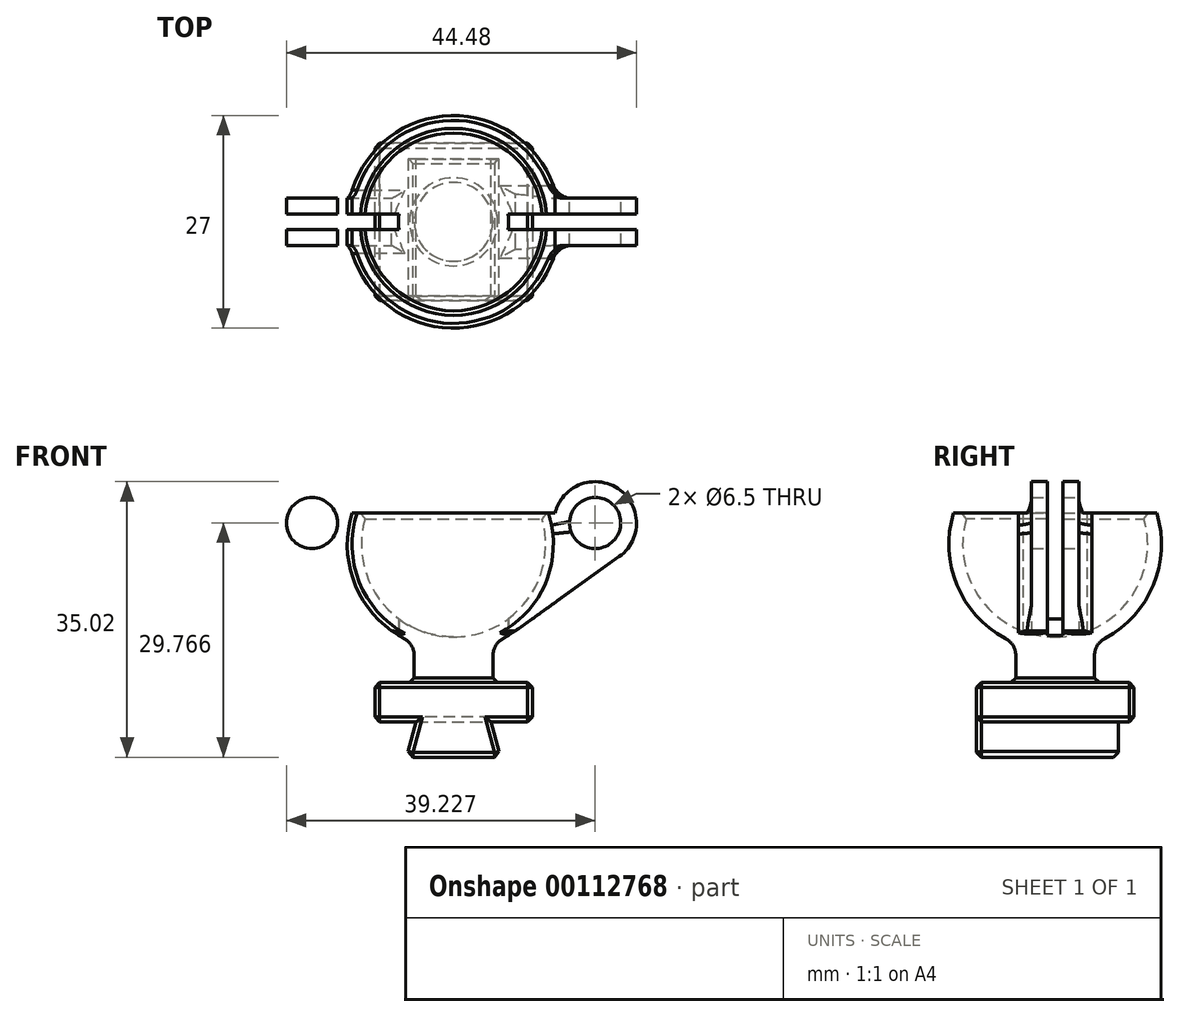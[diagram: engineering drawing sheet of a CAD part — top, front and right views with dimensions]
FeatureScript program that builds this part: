
annotation { "Feature Type Name" : "Feature", "Feature Type Description" : "" }
export const myFeature = defineFeature(function(context is Context, id is Id, definition is map)
    precondition{}
    {
        {
            assignVariable(context, id + "F0", {"name" : "BallWallThickness", "anyValue" : 2});
        }
        {
            assignVariable(context, id + "F1", {"name" : "DovetailBackstopDepth", "anyValue" : 2});
        }
        {
            assignVariable(context, id + "F2", {"name" : "DovetailHeight", "anyValue" : 5});
        }
        {
            assignVariable(context, id + "F3", {"name" : "Thickness", "anyValue" : 20});
        }
        {
            var Q0;
            Q0=qCreatedBy(makeId("Front.planeOp"),FACE);
            var sketch = newSketch(context, id + "F4", { "sketchPlane" : qUnion([Q0])});
            skLineSegment(sketch, "E0", {"start": v(20, 0) * mm, "end": v(20, 5) * mm});
            skLineSegment(sketch, "E1", {"start": v(20, 5) * mm, "end": v(0, 5) * mm});
            skLineSegment(sketch, "E2", {"start": v(5, 5) * mm, "end": v(5, 10) * mm});
            skLineSegment(sketch, "E3", {"start": v(5, 10) * mm, "end": v(15, 10) * mm});
            skLineSegment(sketch, "E4", {"start": v(15, 10) * mm, "end": v(15, 5) * mm});
            skLineSegment(sketch, "E5", {"start": v(10, 5) * mm, "end": v(10, -4.5) * mm, "construction": true});
            skArc(sketch, "E6", {"start": v(-2.9, 26.54) * mm, "mid": v(-2.18, 16.73) * mm, "end": v(5, 10) * mm});
            skPoint(sketch, "E6.centerSnap0", {"position": v(10, 10) * mm});
            skArc(sketch, "E7.trimOffspring", {"start": v(15, 10) * mm, "mid": v(22.18, 16.73) * mm, "end": v(22.9, 26.54) * mm});
            skLineSegment(sketch, "E8", {"start": v(10, 26.54) * mm, "end": v(10, 5) * mm});
            skArc(sketch, "E9", {"start": v(-1.05, 26.54) * mm, "mid": v(10, 10.79) * mm, "end": v(21.05, 26.54) * mm});
            skLineSegment(sketch, "E10", {"start": v(5.25, 0) * mm, "end": v(4.04, -4.5) * mm});
            skLineSegment(sketch, "E11", {"start": v(4.04, -4.5) * mm, "end": v(15.96, -4.5) * mm});
            skLineSegment(sketch, "E12.MirrorCS", {"start": v(14.75, 0) * mm, "end": v(15.96, -4.5) * mm});
            skLineSegment(sketch, "E13", {"start": v(14.75, 0) * mm, "end": v(20, 0) * mm});
            skLineSegment(sketch, "E14", {"start": v(5.25, 0) * mm, "end": v(0, 0) * mm});
            skLineSegment(sketch, "E15", {"start": v(0, 0) * mm, "end": v(0, 5) * mm});
            skLineSegment(sketch, "E16", {"start": v(-3.5, 22.54) * mm, "end": v(23.5, 22.54) * mm, "construction": true});
            skLineSegment(sketch, "E17", {"start": v(22.9, 26.54) * mm, "end": v(-2.9, 26.54) * mm});
            skLineSegment(sketch, "E18", {"start": v(5.25, 0) * mm, "end": v(14.75, 0) * mm});
            skCircle(sketch, "E19", {"center": v(27.99, 25.27) * mm, "radius": 3.25 * mm});
            skArc(sketch, "E20.0", {"start": v(31.04, 21) * mm, "mid": v(30.94, 29.6) * mm, "end": v(22.9, 26.54) * mm});
            skLineSegment(sketch, "E21", {"start": v(31.04, 21) * mm, "end": v(17.86, 11.56) * mm});
            skCircle(sketch, "E22.MirrorC", {"center": v(-7.99, 25.27) * mm, "radius": 3.25 * mm});
            skLineSegment(sketch, "E23.MirrorCS", {"start": v(-11.04, 21) * mm, "end": v(2.14, 11.56) * mm});
            skArc(sketch, "E24.MirrorCS", {"start": v(-11.04, 21) * mm, "mid": v(-10.94, 29.6) * mm, "end": v(-2.9, 26.54) * mm});
            skLineSegment(sketch, "E25", {"start": v(17.86, 11.56) * mm, "end": v(16.84, 12.98) * mm});
            skLineSegment(sketch, "E26.MirrorCS", {"start": v(2.14, 11.56) * mm, "end": v(3.16, 12.98) * mm});
            skSolve(sketch);
        }
        {
            var Q0;
            Q0=makeQuery(id+"F4.imprint","IMPRINT",FACE,{"disambiguationData":[TD([[makeQuery(id+"F4.imprint","IMPRINT",EDGE,{"derivedFrom":sQuery(id+"F4.wireOp",EDGE,"E10")}),1.0]])]});
            extrude(context, id + "F5", {"entities" : qUnion([Q0]), "depth" : (getVariable(context, 'Thickness') / 2) * mm, "hasSecondDirection" : true, "secondDirectionOppositeDirection" : true, "secondDirectionDepth" : (getVariable(context, 'Thickness') / 2 - getVariable(context, 'DovetailBackstopDepth')) * mm});
        }
        {
            var Q0;
            {var subQ4=sQuery(id+"F4.wireOp",EDGE,"E0");Q0=makeQuery(id+"F4.imprint","IMPRINT",FACE,{"disambiguationData":[TD([[makeQuery(id+"F4.imprint","IMPRINT",EDGE,{"derivedFrom":subQ4}),1.0]])]});}
            extrude(context, id + "F6", {"entities" : qUnion([Q0]), "operationType" : NewBodyOperationType.ADD, "depth" : (getVariable(context, 'Thickness')) * mm, "symmetric" : true});
        }
        {
            var Q0;
            {var subQ0=sQuery(id+"F4.wireOp",EDGE,"E2");Q0=makeQuery(id+"F4.imprint","IMPRINT",FACE,{"disambiguationData":[TD([[makeQuery(id+"F4.imprint","IMPRINT",EDGE,{"derivedFrom":subQ0}),-1.0]])]});}
            var Q1;
            Q1=sQuery(id+"F4.wireOp",EDGE,"E8");
            revolve(context, id + "F7", {"operationType" : NewBodyOperationType.ADD, "entities" : qUnion([Q0]), "axis" : qUnion([Q1]), "revolveType" : RevolveType.FULL});
        }
        {
            var Q0;
            Q0=makeQuery(id+"F7.opRevolve","SWEPT_FACE",FACE,{"disambiguationData":[OSD([sQuery(id+"F4.wireOp",EDGE,"E3")])]});
            var sketch = newSketch(context, id + "F8", { "sketchPlane" : qUnion([Q0])});
            skCircle(sketch, "E27", {"center": v(10, 0) * mm, "radius": 13.5 * mm});
            skCircle(sketch, "E28.0", {"center": v(10, 0) * mm, "radius": 5 * mm});
            skLineSegment(sketch, "E29", {"start": v(10, 13.5) * mm, "end": v(10, -13.5) * mm, "construction": true});
            skLineSegment(sketch, "E30", {"start": v(9.5, 13.5) * mm, "end": v(9.5, 6.98) * mm, "construction": true});
            skLineSegment(sketch, "E31.MirrorCS", {"start": v(10.5, 13.5) * mm, "end": v(10.5, 6.98) * mm, "construction": true});
            skLineSegment(sketch, "E32.trimOffspring", {"start": v(9.5, -6.98) * mm, "end": v(9.5, -13.5) * mm, "construction": true});
            skLineSegment(sketch, "E33.trimOffspring", {"start": v(10.5, -6.98) * mm, "end": v(10.5, -13.5) * mm, "construction": true});
            skLineSegment(sketch, "E34", {"start": v(-3.5, 0) * mm, "end": v(23.5, 0) * mm, "construction": true});
            skLineSegment(sketch, "E35", {"start": v(-3.46, 1) * mm, "end": v(3.07, 1) * mm});
            skLineSegment(sketch, "E36.MirrorCS", {"start": v(-3.46, -1) * mm, "end": v(3.07, -1) * mm});
            skLineSegment(sketch, "E37.trimOffspring", {"start": v(16.93, -1) * mm, "end": v(23.46, -1) * mm});
            skLineSegment(sketch, "E38.trimOffspring", {"start": v(16.93, 1) * mm, "end": v(23.46, 1) * mm});
            skCircle(sketch, "E39.0", {"center": v(10, 0) * mm, "radius": 7 * mm});
            skLineSegment(sketch, "E40", {"start": v(-3.46, -1) * mm, "end": v(-33.46, -1) * mm});
            skLineSegment(sketch, "E41", {"start": v(-33.46, -1) * mm, "end": v(-33.46, 1) * mm});
            skLineSegment(sketch, "E42", {"start": v(-33.46, 1) * mm, "end": v(-3.46, 1) * mm});
            skLineSegment(sketch, "E43.MirrorCS", {"start": v(53.46, 1) * mm, "end": v(23.46, 1) * mm});
            skLineSegment(sketch, "E44.MirrorCS", {"start": v(23.46, -1) * mm, "end": v(53.46, -1) * mm});
            skLineSegment(sketch, "E45.MirrorCS", {"start": v(53.46, -1) * mm, "end": v(53.46, 1) * mm});
            skSolve(sketch);
        }
        {
            var Q0;
            {var subQ6=sQuery(id+"F4.wireOp",EDGE,"E6");Q0=makeQuery(id+"F4.imprint","IMPRINT",FACE,{"disambiguationData":[TD([[makeQuery(id+"F4.imprint","IMPRINT",EDGE,{"derivedFrom":subQ6}),1.0]])]});}
            var Q1;
            {var subQ0=sQuery(id+"F4.wireOp",EDGE,"E26.MirrorCS");Q1=makeQuery(id+"F4.imprint","IMPRINT",FACE,{"disambiguationData":[TD([[makeQuery(id+"F4.imprint","IMPRINT",EDGE,{"derivedFrom":subQ0}),-1.0]])]});}
            var Q2;
            Q2=sQuery(id+"F4.wireOp",EDGE,"E8");
            revolve(context, id + "F9", {"operationType" : NewBodyOperationType.ADD, "entities" : qUnion([Q0, Q1]), "axis" : qUnion([Q2]), "revolveType" : RevolveType.FULL});
        }
        {
            var Q0;
            Q0=makeQuery(id+"F4.imprint","IMPRINT",FACE,{"disambiguationData":[TD([[makeQuery(id+"F4.imprint","IMPRINT",EDGE,{"derivedFrom":sQuery(id+"F4.wireOp",EDGE,"E22.MirrorC")}),1.0]])]});
            var Q1;
            {var subQ3=sQuery(id+"F4.wireOp",EDGE,"E26.MirrorCS");Q1=makeQuery(id+"F4.imprint","IMPRINT",FACE,{"disambiguationData":[TD([[makeQuery(id+"F4.imprint","IMPRINT",EDGE,{"derivedFrom":subQ3}),1.0]])]});}
            var Q2;
            {var subQ3=sQuery(id+"F4.wireOp",EDGE,"E25");Q2=makeQuery(id+"F4.imprint","IMPRINT",FACE,{"disambiguationData":[TD([[makeQuery(id+"F4.imprint","IMPRINT",EDGE,{"derivedFrom":subQ3}),-1.0]])]});}
            var Q3;
            Q3=makeQuery(id+"F4.imprint","IMPRINT",FACE,{"disambiguationData":[TD([[makeQuery(id+"F4.imprint","IMPRINT",EDGE,{"derivedFrom":sQuery(id+"F4.wireOp",EDGE,"E19")}),-1.0]])]});
            extrude(context, id + "F10", {"entities" : qUnion([Q0, Q1, Q2, Q3]), "operationType" : NewBodyOperationType.ADD, "depth" : (3 * getVariable(context, 'BallWallThickness')) * mm, "symmetric" : true});
        }
        {
            var Q0;
            {var subQ0=sQuery(id+"F8.wireOp",EDGE,"E35");Q0=makeQuery(id+"F8.imprint","IMPRINT",FACE,{"disambiguationData":[TD([[makeQuery(id+"F8.imprint","IMPRINT",EDGE,{"derivedFrom":subQ0}),-1.0]])]});}
            var Q1;
            {var subQ0=sQuery(id+"F8.wireOp",EDGE,"E32.trimOffspring");Q1=makeQuery(id+"F8.imprint","IMPRINT",FACE,{"disambiguationData":[TD([[makeQuery(id+"F8.imprint","IMPRINT",EDGE,{"derivedFrom":subQ0}),1.0]])]});}
            var Q2;
            {var subQ0=sQuery(id+"F8.wireOp",EDGE,"E37.trimOffspring");Q2=makeQuery(id+"F8.imprint","IMPRINT",FACE,{"disambiguationData":[TD([[makeQuery(id+"F8.imprint","IMPRINT",EDGE,{"derivedFrom":subQ0}),1.0]])]});}
            var Q3;
            {var subQ0=sQuery(id+"F8.wireOp",EDGE,"E30");Q3=makeQuery(id+"F8.imprint","IMPRINT",FACE,{"disambiguationData":[TD([[makeQuery(id+"F8.imprint","IMPRINT",EDGE,{"derivedFrom":subQ0}),1.0]])]});}
            var Q4;
            {var subQ2=sQuery(id+"F8.wireOp",EDGE,"E40");Q4=makeQuery(id+"F8.imprint","IMPRINT",FACE,{"disambiguationData":[TD([[makeQuery(id+"F8.imprint","IMPRINT",EDGE,{"derivedFrom":subQ2}),-1.0]])]});}
            var Q5;
            {var subQ2=sQuery(id+"F8.wireOp",EDGE,"E43.MirrorCS");Q5=makeQuery(id+"F8.imprint","IMPRINT",FACE,{"disambiguationData":[TD([[makeQuery(id+"F8.imprint","IMPRINT",EDGE,{"derivedFrom":subQ2}),1.0]])]});}
            extrude(context, id + "F11", {"entities" : qUnion([Q0, Q1, Q2, Q3, Q4, Q5]), "operationType" : NewBodyOperationType.REMOVE, "depth" : 25 * mm});
        }
        {
            var Q0;
            {var subQ0=sQuery(id+"F4.wireOp",EDGE,"E6");var subQ1=sQuery(id+"F4.wireOp",EDGE,"E3");var subQ2=sQuery(id+"F4.wireOp",EDGE,"E2");Q0=makeQuery(id+"F9.boolean.opBoolean","MERGE",EDGE,{"derivedFrom":[makeQuery(id+"F7.opRevolve","SWEPT_EDGE",EDGE,{"disambiguationData":[OSD([subQ2,subQ1,subQ0])]}),makeQuery(id+"F9.opRevolve","SWEPT_EDGE",EDGE,{"disambiguationData":[OSD([subQ2,subQ1,subQ0])]})]});}
            var Q1;
            Q1=makeQuery(id+"F7.opRevolve","SWEPT_EDGE",EDGE,{"disambiguationData":[OSD([sQuery(id+"F4.wireOp",EDGE,"E1"),sQuery(id+"F4.wireOp",EDGE,"E2")])]});
            var Q2;
            Q2=makeQuery(id+"F10.boolean.opBoolean","INTERSECT",EDGE,{"disambiguationData":[OD(1.0)],"derivedFrom":[makeQuery(id+"F9.opRevolve","SWEPT_FACE",FACE,{"disambiguationData":[OSD([sQuery(id+"F4.wireOp",EDGE,"E6")])]}),makeQuery(id+"F10.opExtrude","SWEPT_FACE",FACE,{"disambiguationData":[OSD([sQuery(id+"F4.wireOp",EDGE,"E26.MirrorCS")])]})]});
            var Q3;
            Q3=makeQuery(id+"F10.boolean.opBoolean","INTERSECT",EDGE,{"disambiguationData":[OD(1.0)],"derivedFrom":[makeQuery(id+"F9.opRevolve","SWEPT_FACE",FACE,{"disambiguationData":[OSD([sQuery(id+"F4.wireOp",EDGE,"E6")])]}),makeQuery(id+"F10.opExtrude","SWEPT_FACE",FACE,{"disambiguationData":[OSD([sQuery(id+"F4.wireOp",EDGE,"E25")])]})]});
            var Q4;
            Q4=makeQuery(id+"F10.boolean.opBoolean","INTERSECT",EDGE,{"disambiguationData":[OD(0.0)],"derivedFrom":[makeQuery(id+"F9.opRevolve","SWEPT_FACE",FACE,{"disambiguationData":[OSD([sQuery(id+"F4.wireOp",EDGE,"E6")])]}),makeQuery(id+"F10.opExtrude","SWEPT_FACE",FACE,{"disambiguationData":[OSD([sQuery(id+"F4.wireOp",EDGE,"E25")])]})]});
            var Q5;
            Q5=makeQuery(id+"F10.boolean.opBoolean","INTERSECT",EDGE,{"disambiguationData":[OD(0.0)],"derivedFrom":[makeQuery(id+"F9.opRevolve","SWEPT_FACE",FACE,{"disambiguationData":[OSD([sQuery(id+"F4.wireOp",EDGE,"E6")])]}),makeQuery(id+"F10.opExtrude","SWEPT_FACE",FACE,{"disambiguationData":[OSD([sQuery(id+"F4.wireOp",EDGE,"E26.MirrorCS")])]})]});
            var Q6;
            Q6=makeQuery(id+"F10.boolean.opBoolean","INTERSECT",EDGE,{"derivedFrom":[makeQuery(id+"F9.opRevolve","SWEPT_FACE",FACE,{"disambiguationData":[OSD([sQuery(id+"F4.wireOp",EDGE,"E6")])]}),makeQuery(id+"F10.opExtrude","CAP_FACE",FACE,{"disambiguationData":[OSD([sQuery(id+"F4.wireOp",EDGE,"E9"),sQuery(id+"F4.wireOp",EDGE,"E17"),sQuery(id+"F4.wireOp",EDGE,"E19"),sQuery(id+"F4.wireOp",EDGE,"E20.0"),sQuery(id+"F4.wireOp",EDGE,"E21"),sQuery(id+"F4.wireOp",EDGE,"E25")])],"isStart":false})]});
            var Q7;
            Q7=makeQuery(id+"F10.boolean.opBoolean","INTERSECT",EDGE,{"derivedFrom":[makeQuery(id+"F9.opRevolve","SWEPT_FACE",FACE,{"disambiguationData":[OSD([sQuery(id+"F4.wireOp",EDGE,"E6")])]}),makeQuery(id+"F10.opExtrude","CAP_FACE",FACE,{"disambiguationData":[OSD([sQuery(id+"F4.wireOp",EDGE,"E9"),sQuery(id+"F4.wireOp",EDGE,"E17"),sQuery(id+"F4.wireOp",EDGE,"E22.MirrorC"),sQuery(id+"F4.wireOp",EDGE,"E23.MirrorCS"),sQuery(id+"F4.wireOp",EDGE,"E24.MirrorCS"),sQuery(id+"F4.wireOp",EDGE,"E26.MirrorCS")])],"isStart":false})]});
            var Q8;
            Q8=makeQuery(id+"F10.boolean.opBoolean","INTERSECT",EDGE,{"derivedFrom":[makeQuery(id+"F9.opRevolve","SWEPT_FACE",FACE,{"disambiguationData":[OSD([sQuery(id+"F4.wireOp",EDGE,"E6")])]}),makeQuery(id+"F10.opExtrude","CAP_FACE",FACE,{"disambiguationData":[OSD([sQuery(id+"F4.wireOp",EDGE,"E9"),sQuery(id+"F4.wireOp",EDGE,"E17"),sQuery(id+"F4.wireOp",EDGE,"E22.MirrorC"),sQuery(id+"F4.wireOp",EDGE,"E23.MirrorCS"),sQuery(id+"F4.wireOp",EDGE,"E24.MirrorCS"),sQuery(id+"F4.wireOp",EDGE,"E26.MirrorCS")])],"isStart":true})]});
            var Q9;
            Q9=makeQuery(id+"F10.boolean.opBoolean","INTERSECT",EDGE,{"derivedFrom":[makeQuery(id+"F9.opRevolve","SWEPT_FACE",FACE,{"disambiguationData":[OSD([sQuery(id+"F4.wireOp",EDGE,"E6")])]}),makeQuery(id+"F10.opExtrude","CAP_FACE",FACE,{"disambiguationData":[OSD([sQuery(id+"F4.wireOp",EDGE,"E9"),sQuery(id+"F4.wireOp",EDGE,"E17"),sQuery(id+"F4.wireOp",EDGE,"E19"),sQuery(id+"F4.wireOp",EDGE,"E20.0"),sQuery(id+"F4.wireOp",EDGE,"E21"),sQuery(id+"F4.wireOp",EDGE,"E25")])],"isStart":true})]});
            fillet(context, id + "F12", {"entities" : qUnion([Q0, Q1, Q2, Q3, Q4, Q5, Q6, Q7, Q8, Q9]), "radius" : (getVariable(context, 'DovetailHeight') / 2) * mm, "tangentPropagation" : true, "allowEdgeOverflow" : false});
        }
        {
            var Q0;
            {var subQ0=sQuery(id+"F4.wireOp",EDGE,"E18");Q0=makeQuery(id+"F6.boolean.opBoolean","MERGE",FACE,{"derivedFrom":[makeQuery(id+"F5.opExtrude","CAP_FACE",FACE,{"disambiguationData":[OSD([sQuery(id+"F4.wireOp",EDGE,"E10"),sQuery(id+"F4.wireOp",EDGE,"E11"),sQuery(id+"F4.wireOp",EDGE,"E12.MirrorCS"),subQ0])],"isStart":false}),makeQuery(id+"F6.opExtrude","CAP_FACE",FACE,{"disambiguationData":[OSD([sQuery(id+"F4.wireOp",EDGE,"E0"),sQuery(id+"F4.wireOp",EDGE,"E1"),sQuery(id+"F4.wireOp",EDGE,"E13"),sQuery(id+"F4.wireOp",EDGE,"E14"),sQuery(id+"F4.wireOp",EDGE,"E15"),subQ0])],"isStart":false})]});}
            var Q1;
            Q1=makeQuery(id+"F6.opExtrude","SWEPT_FACE",FACE,{"disambiguationData":[OSD([sQuery(id+"F4.wireOp",EDGE,"E15")])]});
            var Q2;
            Q2=makeQuery(id+"F6.opExtrude","CAP_FACE",FACE,{"disambiguationData":[OSD([sQuery(id+"F4.wireOp",EDGE,"E0"),sQuery(id+"F4.wireOp",EDGE,"E1"),sQuery(id+"F4.wireOp",EDGE,"E13"),sQuery(id+"F4.wireOp",EDGE,"E14"),sQuery(id+"F4.wireOp",EDGE,"E15"),sQuery(id+"F4.wireOp",EDGE,"E18")])],"isStart":true});
            var Q3;
            Q3=makeQuery(id+"F6.opExtrude","SWEPT_FACE",FACE,{"disambiguationData":[OSD([sQuery(id+"F4.wireOp",EDGE,"E0")])]});
            var Q4;
            Q4=makeQuery(id+"F5.opExtrude","SWEPT_FACE",FACE,{"disambiguationData":[OSD([sQuery(id+"F4.wireOp",EDGE,"E11")])]});
            var Q5;
            Q5=makeQuery(id+"F6.opExtrude","SWEPT_FACE",FACE,{"disambiguationData":[OSD([sQuery(id+"F4.wireOp",EDGE,"E1")])]});
            var Q6;
            {var subQ0=sQuery(id+"F4.wireOp",EDGE,"E9");var subQ1=sQuery(id+"F4.wireOp",EDGE,"E17");Q6=makeQuery(id+"F11.boolean.opBoolean","SPLIT",EDGE,{"disambiguationData":[TD([makeQuery(id+"F11.opExtrude","SWEPT_FACE",FACE,{"disambiguationData":[OSD([sQuery(id+"F8.wireOp",EDGE,"E30")])]})])],"derivedFrom":makeQuery(id+"F9.opRevolve","SWEPT_EDGE",EDGE,{"disambiguationData":[OSD([subQ0,subQ1])]})});}
            var Q7;
            {var subQ0=sQuery(id+"F4.wireOp",EDGE,"E9");var subQ1=sQuery(id+"F4.wireOp",EDGE,"E17");Q7=makeQuery(id+"F11.boolean.opBoolean","SPLIT",EDGE,{"disambiguationData":[TD([makeQuery(id+"F11.opExtrude","SWEPT_FACE",FACE,{"disambiguationData":[OSD([sQuery(id+"F8.wireOp",EDGE,"E32.trimOffspring")])]})])],"derivedFrom":makeQuery(id+"F9.opRevolve","SWEPT_EDGE",EDGE,{"disambiguationData":[OSD([subQ0,subQ1])]})});}
            var Q8;
            {var subQ0=sQuery(id+"F4.wireOp",EDGE,"E9");var subQ1=sQuery(id+"F4.wireOp",EDGE,"E17");Q8=makeQuery(id+"F11.boolean.opBoolean","SPLIT",EDGE,{"disambiguationData":[TD([makeQuery(id+"F11.opExtrude","SWEPT_FACE",FACE,{"disambiguationData":[OSD([sQuery(id+"F8.wireOp",EDGE,"E33.trimOffspring")])]})])],"derivedFrom":makeQuery(id+"F9.opRevolve","SWEPT_EDGE",EDGE,{"disambiguationData":[OSD([subQ0,subQ1])]})});}
            var Q9;
            {var subQ0=sQuery(id+"F4.wireOp",EDGE,"E9");var subQ1=sQuery(id+"F4.wireOp",EDGE,"E17");Q9=makeQuery(id+"F11.boolean.opBoolean","SPLIT",EDGE,{"disambiguationData":[TD([makeQuery(id+"F11.opExtrude","SWEPT_FACE",FACE,{"disambiguationData":[OSD([sQuery(id+"F8.wireOp",EDGE,"E31.MirrorCS")])]})])],"derivedFrom":makeQuery(id+"F9.opRevolve","SWEPT_EDGE",EDGE,{"disambiguationData":[OSD([subQ0,subQ1])]})});}
            var Q10;
            {var subQ0=sQuery(id+"F4.wireOp",EDGE,"E17");var subQ1=sQuery(id+"F4.wireOp",EDGE,"E9");Q10=makeQuery(id+"F11.boolean.opBoolean","SPLIT",EDGE,{"disambiguationData":[TD([makeQuery(id+"F11.opExtrude","SWEPT_FACE",FACE,{"disambiguationData":[OSD([sQuery(id+"F8.wireOp",EDGE,"E36.MirrorCS"),sQuery(id+"F8.wireOp",EDGE,"E40")])]})])],"derivedFrom":makeQuery(id+"F9.opRevolve","SWEPT_EDGE",EDGE,{"disambiguationData":[OSD([subQ1,subQ0])]})});}
            var Q11;
            {var subQ0=sQuery(id+"F4.wireOp",EDGE,"E17");var subQ1=sQuery(id+"F4.wireOp",EDGE,"E9");Q11=makeQuery(id+"F11.boolean.opBoolean","SPLIT",EDGE,{"disambiguationData":[TD([makeQuery(id+"F11.opExtrude","SWEPT_FACE",FACE,{"disambiguationData":[OSD([sQuery(id+"F8.wireOp",EDGE,"E35"),sQuery(id+"F8.wireOp",EDGE,"E42")])]})])],"derivedFrom":makeQuery(id+"F9.opRevolve","SWEPT_EDGE",EDGE,{"disambiguationData":[OSD([subQ1,subQ0])]})});}
            chamfer(context, id + "F13", {"entities" : qUnion([Q0, Q1, Q2, Q3, Q4, Q5, Q6, Q7, Q8, Q9, Q10, Q11]), "width" : 0.6 * mm, "tangentPropagation" : true});
        }
    });
